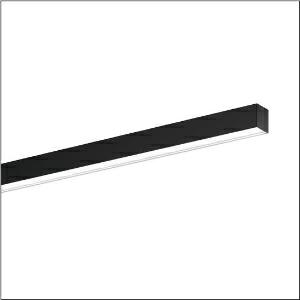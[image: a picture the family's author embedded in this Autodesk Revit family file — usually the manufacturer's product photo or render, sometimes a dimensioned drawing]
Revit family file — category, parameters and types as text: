
# Revit family: silica_r__21_51mx23db35bb_4e5d
name_source: partatom
category: Lighting Fixtures
units: mm (PartAtom-declared; Revit-internal decimal feet)

## family parameters
Cut with Voids When Loaded = No
Host = Face
Light Source = No
Part Type = Normal
Room Calculation Point = No
Round Connector Dimension = Use Diameter
Shared = No

## types (1)
- --- (1 x LED, 4100 lm, 30.1 W, 3000K)
    Apparent Load = 30 VA
    CIE Flux Codes = 78 96 99 100 100
    Color Rendering = 80
    Color Temperature = 3000K
    Default Elevation = 1800 mm
    Description = Silica® 21, office luminaire, primary optical cover: prismatic diffuser, of PMMA, CAT 2 (L<= 3000cd/m²), light emission: direct distribution, primary light characteristic: symmetric, installation type: surface-mounted, LED, rated luminous flux: 4.100lm, luminous efficacy: 136lm/W, light colour: 830, colour temperature: 3000K, with terminal, 3+2-pole, max. 2.5mm², mains connection: 220..240V, AC, 50/60Hz, rated input power: 30.1W, luminaire housing, of aluminium, jet black (RAL 9005), length: 1.504mm, width: 53mm, height: 53mm, protection rating (complete): IP20, insulation class (complete): insulation class I (protective earthing), certification: CE, permissible operating ambient temperature: 0..+35°C, standard: EN 50419, packaging unit: 1 piece
    Height = 0 mm  [stored 0 ft]
    Lamp = 1 x LED
    Lamp Light Flux = 4100 lm
    Lamp Power = 30.1 W
    Lamp count = 1
    Length = 1504 mm
    Luminous efficacy = 136 lm/W
    Manufacturer = Siteco
    ModVariant = No
    Model = 51MX23DB35BB
    Mounting Place = Ceiling
    Mounting Type = Recessed
    Number of Poles = 1
    OnlyDefault = Yes
    Power Factor = 1
    Product Name = Silica® 21
    Product group = office luminaire | ceiling recessed
    ProductGroupID = 401
    Protection Class = Protection class I
    Protection Degree = IP 20
    RLX_Detail_Level = 1
    RLX_Emergency_Light_Flux = 0 lm
    RLX_Emergency_Type = 0
    RLX_Emergency_Type_DB = No
    RlxData = <blob elided: 23745 chars, md5=c663599a>
    Socket = socket
    Standby Power = 0 W
    System Light Flux = 4100 lm
    System Power = 30 W
    Type Comments = factory setting: luminous flux: 100 % | dim-lin: 254 | 345 mA
    Type Image = l_1297760.jpg
    URL = http://relux.com
    VarID = @adj_049907
    Voltage = 0 V
    Weight = 0.00 kg
    Width = 53 mm

note: [stored X ft] marks values corroborated as IEEE doubles in the binary element streams (Revit-internal decimal feet)

## geometry (parser evidence)
native form markers: Blend x4, Sweep x11
no freeform markers — native parametric forms only
